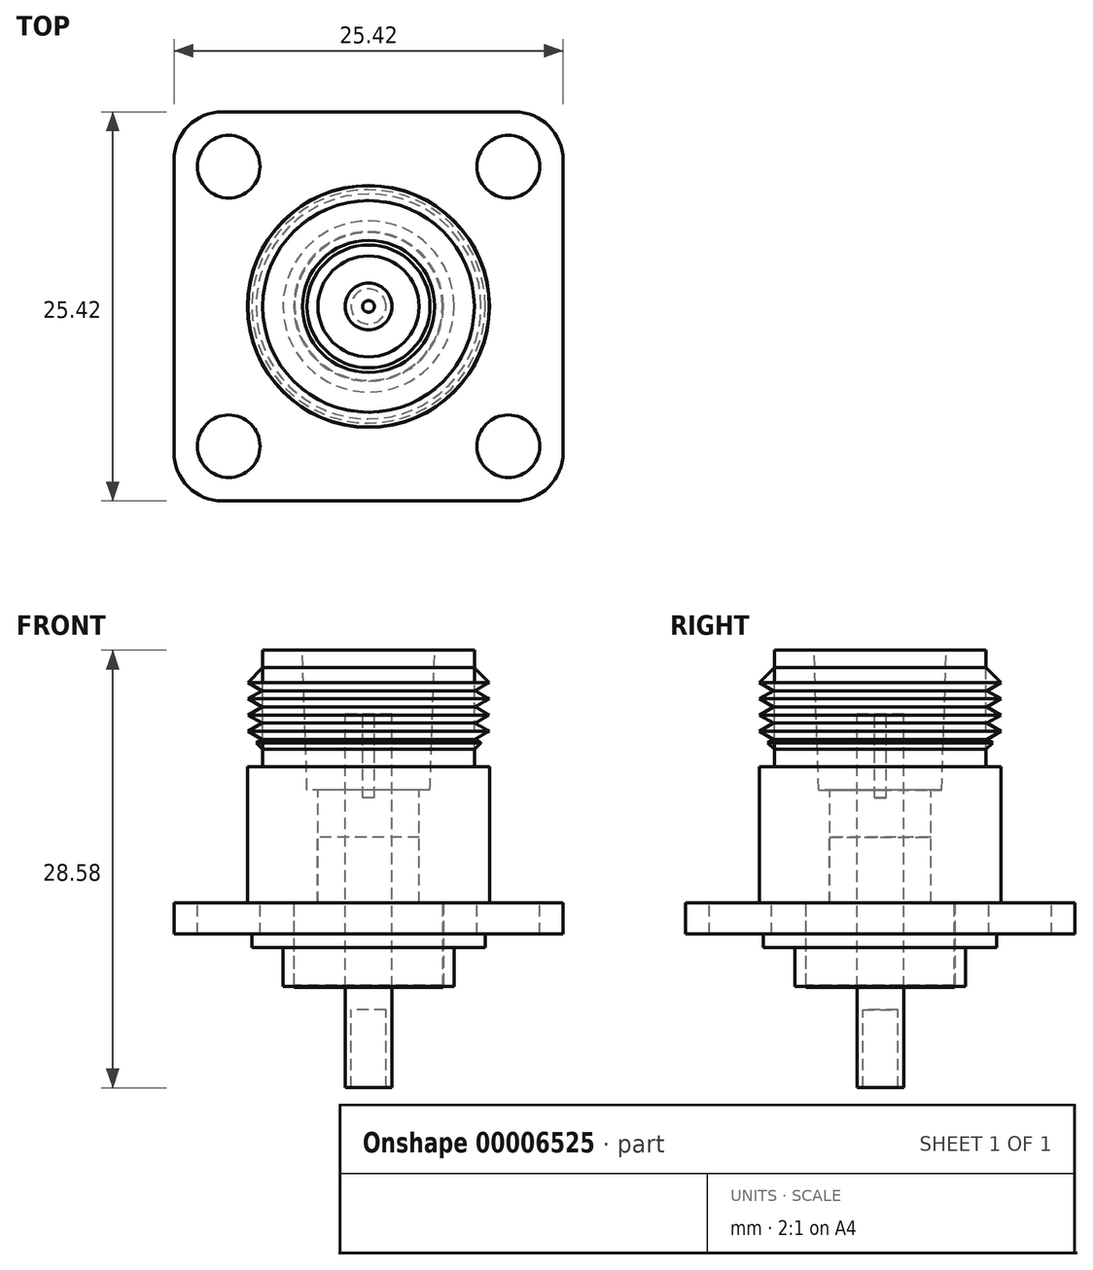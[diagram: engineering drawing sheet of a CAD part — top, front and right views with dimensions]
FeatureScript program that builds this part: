
annotation { "Feature Type Name" : "Feature", "Feature Type Description" : "" }
export const myFeature = defineFeature(function(context is Context, id is Id, definition is map)
    precondition{}
    {
        {
            var Q0;
            Q0=qCreatedBy(makeId("Top.planeOp"),FACE);
            var sketch = newSketch(context, id + "F0", { "sketchPlane" : qUnion([Q0])});
            skLineSegment(sketch, "E0", {"start": v(-32.66, 0) * mm, "end": v(40.56, 0) * mm, "construction": true});
            skLineSegment(sketch, "E1", {"start": v(0, 23.26) * mm, "end": v(0, -23.07) * mm, "construction": true});
            skLineSegment(sketch, "E2.rect.bottom", {"start": v(9.54, 12.71) * mm, "end": v(-9.54, 12.71) * mm});
            skLineSegment(sketch, "E2.rect.top", {"start": v(9.54, -12.71) * mm, "end": v(-9.54, -12.71) * mm});
            skLineSegment(sketch, "E2.rect.left", {"start": v(12.71, 9.54) * mm, "end": v(12.71, -9.54) * mm});
            skLineSegment(sketch, "E2.rect.right", {"start": v(-12.71, 9.54) * mm, "end": v(-12.71, -9.54) * mm});
            skPoint(sketch, "E2.rect.middle", {"position": v(0, 0) * mm});
            skCircle(sketch, "E3", {"center": v(9.13, 9.13) * mm, "radius": 2.05 * mm});
            skCircle(sketch, "E4.0.MirrorC", {"center": v(-9.13, 9.13) * mm, "radius": 2.05 * mm});
            skCircle(sketch, "E5.0.MirrorC", {"center": v(9.13, -9.13) * mm, "radius": 2.05 * mm});
            skCircle(sketch, "E6.0.MirrorC", {"center": v(-9.13, -9.13) * mm, "radius": 2.05 * mm});
            skPoint(sketch, "E7.visualSharp", {"position": v(-12.71, 12.71) * mm});
            skArc(sketch, "E7.filletArc", {"start": v(-9.54, 12.71) * mm, "mid": v(-11.78, 11.78) * mm, "end": v(-12.71, 9.54) * mm});
            skPoint(sketch, "E8.0.MirrorP", {"position": v(12.71, 12.71) * mm});
            skArc(sketch, "E9.filletArc", {"start": v(12.71, 9.54) * mm, "mid": v(11.78, 11.78) * mm, "end": v(9.54, 12.71) * mm});
            skPoint(sketch, "E10.visualSharp", {"position": v(12.71, -12.71) * mm});
            skArc(sketch, "E10.filletArc", {"start": v(9.54, -12.71) * mm, "mid": v(11.78, -11.78) * mm, "end": v(12.71, -9.54) * mm});
            skPoint(sketch, "E11.visualSharp", {"position": v(-12.71, -12.71) * mm});
            skArc(sketch, "E11.filletArc", {"start": v(-12.71, -9.54) * mm, "mid": v(-11.78, -11.78) * mm, "end": v(-9.54, -12.71) * mm});
            skSolve(sketch);
        }
        {
            var Q0;
            Q0 = qSketchRegion(id + "F0", true);
            var Q1;
            Q1 = qSketchRegion(id + "F2", true);
            extrude(context, id + "F1", {"entities" : qUnion([Q0, Q1]), "oppositeDirection" : true, "depth" : 2.03 * mm});
        }
        {
            var Q0;
            Q0=qCreatedBy(makeId("Right.planeOp"),FACE);
            var sketch = newSketch(context, id + "F2", { "sketchPlane" : qUnion([Q0])});
            skLineSegment(sketch, "E12", {"start": v(0, 38.13) * mm, "end": v(0, -57.33) * mm, "construction": true});
            skLineSegment(sketch, "E13", {"start": v(7.62, 0) * mm, "end": v(7.62, -2.91) * mm});
            skLineSegment(sketch, "E14", {"start": v(7.62, -2.91) * mm, "end": v(5.59, -2.91) * mm});
            skLineSegment(sketch, "E15", {"start": v(5.59, -2.91) * mm, "end": v(5.59, -5.46) * mm});
            skLineSegment(sketch, "E16", {"start": v(5.59, -5.46) * mm, "end": v(4.83, -5.46) * mm});
            skLineSegment(sketch, "E17", {"start": v(4.83, -5.46) * mm, "end": v(4.83, 0) * mm});
            skLineSegment(sketch, "E18", {"start": v(4.83, 0) * mm, "end": v(7.62, 0) * mm});
            skSolve(sketch);
        }
        {
            var Q0;
            Q0 = qSketchRegion(id + "F2", true);
            var Q1;
            Q1=sQuery(id+"F2.wireOp",EDGE,"E12");
            revolve(context, id + "F3", {"operationType" : NewBodyOperationType.ADD, "entities" : qUnion([Q0]), "axis" : qUnion([Q1]), "revolveType" : RevolveType.FULL});
        }
        {
            var Q0;
            Q0=qCreatedBy(makeId("Right.planeOp"),FACE);
            var sketch = newSketch(context, id + "F4", { "sketchPlane" : qUnion([Q0])});
            skLineSegment(sketch, "E19", {"start": v(0, 27.56) * mm, "end": v(0, -14.21) * mm, "construction": true});
            skLineSegment(sketch, "E20", {"start": v(7.9, 0) * mm, "end": v(7.9, 8.9) * mm});
            skLineSegment(sketch, "E21", {"start": v(7.9, 8.9) * mm, "end": v(6.9, 8.9) * mm});
            skLineSegment(sketch, "E22", {"start": v(6.9, 8.9) * mm, "end": v(6.9, 16.51) * mm});
            skLineSegment(sketch, "E23", {"start": v(6.9, 16.51) * mm, "end": v(4.32, 16.51) * mm});
            skLineSegment(sketch, "E24", {"start": v(4.32, 16.51) * mm, "end": v(4.01, 7.4) * mm});
            skLineSegment(sketch, "E25", {"start": v(4.01, 7.4) * mm, "end": v(3.3, 7.4) * mm});
            skLineSegment(sketch, "E26", {"start": v(3.3, 7.4) * mm, "end": v(3.3, 0) * mm});
            skLineSegment(sketch, "E27", {"start": v(3.3, 0) * mm, "end": v(7.9, 0) * mm});
            skSolve(sketch);
        }
        {
            var Q0;
            Q0 = qSketchRegion(id + "F4", true);
            var Q1;
            Q1=sQuery(id+"F4.wireOp",EDGE,"E19");
            revolve(context, id + "F5", {"operationType" : NewBodyOperationType.ADD, "entities" : qUnion([Q0]), "axis" : qUnion([Q1]), "revolveType" : RevolveType.FULL});
        }
        {
            var Q0;
            Q0=qCreatedBy(makeId("Right.planeOp"),FACE);
            var sketch = newSketch(context, id + "F6", { "sketchPlane" : qUnion([Q0])});
            skLineSegment(sketch, "E28", {"start": v(0, 35.83) * mm, "end": v(0, -34.84) * mm, "construction": true});
            skLineSegment(sketch, "E29", {"start": v(4.88, 0) * mm, "end": v(4.88, -5.38) * mm});
            skLineSegment(sketch, "E30", {"start": v(4.88, -5.38) * mm, "end": v(0, -5.38) * mm});
            skLineSegment(sketch, "E31", {"start": v(0, -5.38) * mm, "end": v(0, 0) * mm});
            skLineSegment(sketch, "E32", {"start": v(0, 0) * mm, "end": v(4.88, 0) * mm});
            skSolve(sketch);
        }
        {
            var Q0;
            Q0 = qSketchRegion(id + "F6", true);
            var Q1;
            Q1=sQuery(id+"F6.wireOp",EDGE,"E28");
            revolve(context, id + "F7", {"operationType" : NewBodyOperationType.REMOVE, "entities" : qUnion([Q0]), "axis" : qUnion([Q1]), "revolveType" : RevolveType.FULL, "oppositeDirection" : true});
        }
        {
            var Q0;
            Q0=qCreatedBy(makeId("Right.planeOp"),FACE);
            var sketch = newSketch(context, id + "F8", { "sketchPlane" : qUnion([Q0])});
            skLineSegment(sketch, "E33", {"start": v(0, 30.77) * mm, "end": v(0, -24.02) * mm});
            skLineSegment(sketch, "E34", {"start": v(4.85, 0) * mm, "end": v(4.85, -5.51) * mm});
            skLineSegment(sketch, "E35", {"start": v(4.85, -5.51) * mm, "end": v(0, -5.51) * mm});
            skLineSegment(sketch, "E36", {"start": v(0, -5.51) * mm, "end": v(0, 4.3) * mm});
            skLineSegment(sketch, "E37", {"start": v(0, 4.3) * mm, "end": v(3.32, 4.3) * mm});
            skLineSegment(sketch, "E38", {"start": v(3.32, 4.3) * mm, "end": v(3.32, 0) * mm});
            skLineSegment(sketch, "E39", {"start": v(3.32, 0) * mm, "end": v(4.85, 0) * mm});
            skSolve(sketch);
        }
        {
            var Q0;
            Q0 = qSketchRegion(id + "F8", true);
            var Q1;
            Q1=sQuery(id+"F8.wireOp",EDGE,"E33");
            revolve(context, id + "F9", {"entities" : qUnion([Q0]), "axis" : qUnion([Q1]), "revolveType" : RevolveType.FULL});
        }
        {
            var Q0;
            Q0=qCreatedBy(makeId("Right.planeOp"),FACE);
            var sketch = newSketch(context, id + "F10", { "sketchPlane" : qUnion([Q0])});
            skLineSegment(sketch, "E40", {"start": v(0, 39.59) * mm, "end": v(0, -42.33) * mm, "construction": true});
            skLineSegment(sketch, "E41", {"start": v(0, 6.86) * mm, "end": v(0.38, 6.86) * mm});
            skLineSegment(sketch, "E42", {"start": v(0.38, 6.86) * mm, "end": v(0.38, 12.32) * mm});
            skLineSegment(sketch, "E43", {"start": v(0.38, 12.32) * mm, "end": v(1.52, 12.32) * mm});
            skLineSegment(sketch, "E44", {"start": v(1.52, 12.32) * mm, "end": v(1.52, -12.07) * mm});
            skLineSegment(sketch, "E45", {"start": v(1.52, -12.07) * mm, "end": v(1.14, -12.07) * mm});
            skLineSegment(sketch, "E46", {"start": v(1.14, -12.07) * mm, "end": v(1.14, -6.99) * mm});
            skLineSegment(sketch, "E47", {"start": v(1.14, -6.99) * mm, "end": v(0, -6.99) * mm});
            skLineSegment(sketch, "E48", {"start": v(0, 6.86) * mm, "end": v(0, -6.99) * mm});
            skSolve(sketch);
        }
        {
            var Q0;
            Q0=makeQuery(id+"F10.imprint","IMPRINT",FACE,{"disambiguationData":[TD([[makeQuery(id+"F10.imprint","IMPRINT",EDGE,{"derivedFrom":sQuery(id+"F10.wireOp",EDGE,"E41")}),-1.0]])]});
            var Q1;
            Q1=sQuery(id+"F10.wireOp",EDGE,"E40");
            revolve(context, id + "F11", {"entities" : qUnion([Q0]), "axis" : qUnion([Q1]), "revolveType" : RevolveType.FULL});
        }
        {
            var Q0;
            Q0=qCreatedBy(makeId("Right.planeOp"),FACE);
            var sketch = newSketch(context, id + "F12", { "sketchPlane" : qUnion([Q0])});
            skLineSegment(sketch, "E49", {"start": v(0, 18.76) * mm, "end": v(0, 5.5) * mm, "construction": true});
            skLineSegment(sketch, "E50", {"start": v(7.87, 17.2) * mm, "end": v(7.87, 9) * mm, "construction": true});
            skLineSegment(sketch, "E51", {"start": v(6.9, 18.19) * mm, "end": v(6.9, 6.96) * mm, "construction": true});
            skLineSegment(sketch, "E52", {"start": v(6.1, 15.37) * mm, "end": v(9.18, 15.37) * mm, "construction": true});
            skLineSegment(sketch, "E53", {"start": v(5.9, 10.03) * mm, "end": v(9.16, 10.03) * mm, "construction": true});
            skLineSegment(sketch, "E54", {"start": v(6.9, 15.37) * mm, "end": v(7.87, 14.4) * mm});
            skLineSegment(sketch, "E55", {"start": v(7.87, 14.4) * mm, "end": v(7.87, 10.17) * mm, "construction": true});
            skLineSegment(sketch, "E56", {"start": v(7.35, 10.47) * mm, "end": v(6.9, 10.03) * mm});
            skLineSegment(sketch, "E57", {"start": v(6.9, 10.03) * mm, "end": v(6.9, 15.37) * mm});
            skLineSegment(sketch, "E58", {"start": v(7.87, 14.4) * mm, "end": v(6.96, 13.87) * mm});
            skLineSegment(sketch, "E59", {"start": v(6.96, 13.87) * mm, "end": v(7.87, 13.34) * mm});
            skLineSegment(sketch, "E60.0.1.0", {"start": v(7.87, 13.34) * mm, "end": v(6.96, 12.81) * mm});
            skLineSegment(sketch, "E60.0.1.1", {"start": v(6.96, 12.81) * mm, "end": v(7.87, 12.29) * mm});
            skLineSegment(sketch, "E60.0.2.0", {"start": v(7.87, 12.29) * mm, "end": v(6.96, 11.76) * mm});
            skLineSegment(sketch, "E60.0.2.1", {"start": v(6.96, 11.76) * mm, "end": v(7.87, 11.23) * mm});
            skLineSegment(sketch, "E60.0.3.0", {"start": v(7.87, 11.23) * mm, "end": v(6.96, 10.7) * mm});
            skLineSegment(sketch, "E60.0.3.1", {"start": v(6.96, 10.7) * mm, "end": v(7.35, 10.47) * mm});
            skLineSegment(sketch, "E60.direction1", {"start": v(6.96, 13.87) * mm, "end": v(32.36, 13.87) * mm, "construction": true});
            skLineSegment(sketch, "E60.direction2", {"start": v(6.96, 13.87) * mm, "end": v(6.96, 12.81) * mm, "construction": true});
            skPoint(sketch, "E61.orphan", {"position": v(7.87, 10.17) * mm});
            skSolve(sketch);
        }
        {
            var Q0;
            Q0=makeQuery(id+"F12.imprint","IMPRINT",FACE,{"disambiguationData":[TD([[makeQuery(id+"F12.imprint","IMPRINT",EDGE,{"derivedFrom":sQuery(id+"F12.wireOp",EDGE,"E54")}),-1.0]])]});
            var Q1;
            Q1=sQuery(id+"F12.wireOp",EDGE,"E55");
            var Q2;
            Q2=sQuery(id+"F12.wireOp",EDGE,"E49");
            revolve(context, id + "F13", {"entities" : qUnion([Q0]), "surfaceEntities" : qUnion([Q1]), "axis" : qUnion([Q2]), "revolveType" : RevolveType.FULL});
        }
    });
